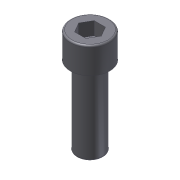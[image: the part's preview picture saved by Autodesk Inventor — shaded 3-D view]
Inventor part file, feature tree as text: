
AUTODESK INVENTOR PART (.ipt)
format: ipt  version: 2012 (Build 160160000, 160)  size: 110,592 bytes
history: native  units: in
note: dims shown in document units (in); Inventor stores cm internally (conversion verified against a paired STEP export)
features: extrude x3, sketch x3, fillet x1
ambient origin geometry x8: Origin, YZ Plane, XZ Plane, XY Plane, X Axis, Y Axis, Z Axis, Center Point
bodies: Solid1 (feature_tree)
feature tree (7):
  extrude  "Extrusion1"  Depth=0.75in TaperAngle=0.0deg
  extrude  "Extrusion2"  Depth=0.25in TaperAngle=0.0deg
  extrude  "Extrusion3"  Depth=0.125in TaperAngle=0.0deg
  fillet  "Fillet1"  Radius=0.0156in
  sketch  "Sketch1"  dims[d0=0.25in d1=0.75in d2=0.0in]
  sketch  "Sketch2"  dims[d3=0.375in d4=0.25in d5=0.0in]
  sketch  "Sketch3"  dims[d6=0.1875in d7=0.125in d8=0.0in d9=0.0156in]
